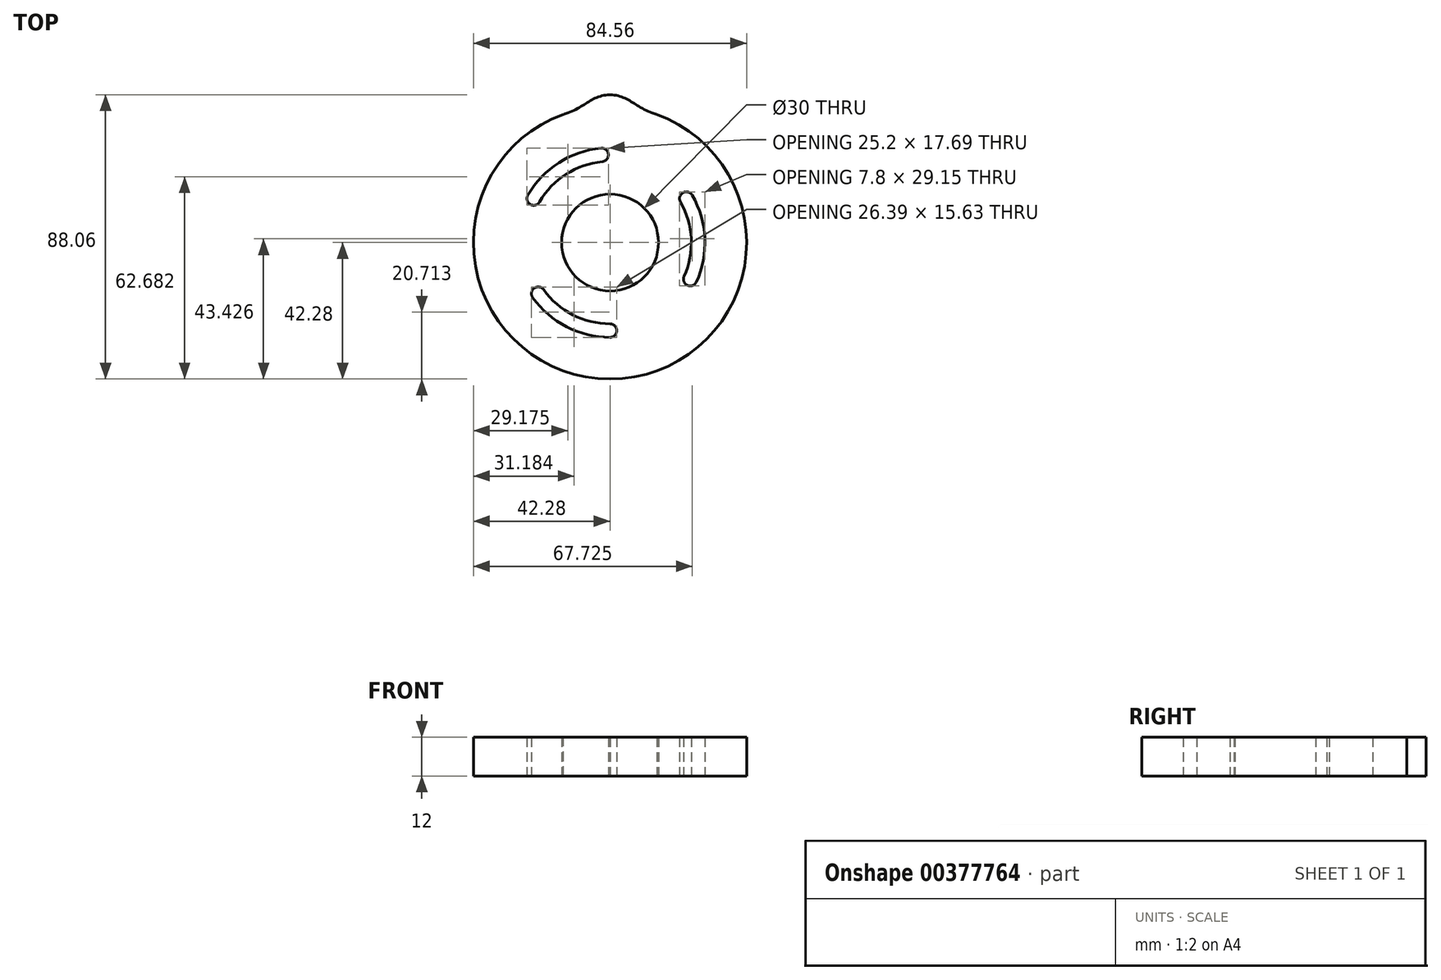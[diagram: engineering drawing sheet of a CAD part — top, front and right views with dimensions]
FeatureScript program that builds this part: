
annotation { "Feature Type Name" : "Feature", "Feature Type Description" : "" }
export const myFeature = defineFeature(function(context is Context, id is Id, definition is map)
    precondition{}
    {
        {
            var Q0;
            Q0=qCreatedBy(makeId("Top.planeOp"),FACE);
            var sketch = newSketch(context, id + "F0", { "sketchPlane" : qUnion([Q0])});
            skCircle(sketch, "E0", {"center": v(0, 0) * mm, "radius": 42.28 * mm});
            skCircle(sketch, "E1", {"center": v(0, 0) * mm, "radius": 15 * mm});
            skLineSegment(sketch, "E2", {"start": v(0, 42.28) * mm, "end": v(0, -42.28) * mm, "construction": true});
            skLineSegment(sketch, "E3", {"start": v(0, 0) * mm, "end": v(-14.46, 39.73) * mm, "construction": true});
            skLineSegment(sketch, "E4", {"start": v(0, 0) * mm, "end": v(14.46, 39.73) * mm, "construction": true});
            skLineSegment(sketch, "E5", {"start": v(0, 42.28) * mm, "end": v(0, 45.78) * mm, "construction": true});
            skFitSpline(sketch, "E6", {"points": [v(0, 45.78) * mm, v(-14.46, 39.73) * mm], "startDerivative": vector(-17.86, -0.27) * mm, "endDerivative": vector(-19.75, -5.43) * mm});
            skFitSpline(sketch, "E7.MirrorCS", {"points": [v(0, 45.78) * mm, v(14.46, 39.73) * mm], "startDerivative": vector(17.86, -0.27) * mm, "endDerivative": vector(19.75, -5.43) * mm});
            skLineSegment(sketch, "E8", {"start": v(0, 0) * mm, "end": v(36.61, 21.14) * mm, "construction": true});
            skLineSegment(sketch, "E9", {"start": v(0, 0) * mm, "end": v(-36.45, 21.04) * mm, "construction": true});
            skArc(sketch, "E10", {"start": v(-23.62, 13.64) * mm, "mid": v(-14.75, 22.95) * mm, "end": v(-2.6, 27.16) * mm, "construction": true});
            skArc(sketch, "E11", {"start": v(23.62, 13.64) * mm, "mid": v(27.25, 1.3) * mm, "end": v(24.81, -11.33) * mm, "construction": true});
            skArc(sketch, "E12", {"start": v(0, -27.28) * mm, "mid": v(-12.5, -24.25) * mm, "end": v(-22.22, -15.82) * mm, "construction": true});
            skArc(sketch, "E13.0.startCap", {"start": v(-21.8, 12.59) * mm, "mid": v(-24.67, 11.82) * mm, "end": v(-25.44, 14.69) * mm});
            skArc(sketch, "E13.0.endCap", {"start": v(-2.8, 29.25) * mm, "mid": v(-0.5, 27.36) * mm, "end": v(-2.4, 25.07) * mm});
            skArc(sketch, "E13.0.left", {"start": v(-25.44, 14.69) * mm, "mid": v(-15.88, 24.72) * mm, "end": v(-2.8, 29.25) * mm});
            skArc(sketch, "E13.0.right", {"start": v(-21.8, 12.59) * mm, "mid": v(-13.61, 21.18) * mm, "end": v(-2.4, 25.07) * mm});
            skArc(sketch, "E13.1.startCap", {"start": v(21.8, 12.59) * mm, "mid": v(22.57, 15.46) * mm, "end": v(25.44, 14.69) * mm});
            skArc(sketch, "E13.1.endCap", {"start": v(26.72, -12.2) * mm, "mid": v(23.94, -13.24) * mm, "end": v(22.9, -10.46) * mm});
            skArc(sketch, "E13.1.left", {"start": v(25.44, 14.69) * mm, "mid": v(29.35, 1.4) * mm, "end": v(26.72, -12.2) * mm});
            skArc(sketch, "E13.1.right", {"start": v(21.8, 12.59) * mm, "mid": v(25.15, 1.2) * mm, "end": v(22.9, -10.46) * mm});
            skArc(sketch, "E13.2.startCap", {"start": v(0, -25.18) * mm, "mid": v(2.1, -27.28) * mm, "end": v(0, -29.38) * mm});
            skArc(sketch, "E13.2.endCap", {"start": v(-23.93, -17.04) * mm, "mid": v(-23.44, -14.11) * mm, "end": v(-20.51, -14.6) * mm});
            skArc(sketch, "E13.2.left", {"start": v(0, -29.38) * mm, "mid": v(-13.46, -26.11) * mm, "end": v(-23.93, -17.04) * mm});
            skArc(sketch, "E13.2.right", {"start": v(0, -25.18) * mm, "mid": v(-11.54, -22.38) * mm, "end": v(-20.51, -14.6) * mm});
            skSolve(sketch);
        }
        {
            var Q0;
            Q0=makeQuery(id+"F0.imprint","IMPRINT",FACE,{"disambiguationData":[TD([[makeQuery(id+"F0.imprint","IMPRINT",EDGE,{"derivedFrom":sQuery(id+"F0.wireOp",EDGE,"E1")}),-1.0]])]});
            var Q1;
            {var subQ0=sQuery(id+"F0.wireOp",EDGE,"E7.MirrorCS");var subQ1=sQuery(id+"F0.wireOp",EDGE,"E0");var subQ2=makeQuery(id+"F0.imprint","INTERSECT",VERTEX,{"disambiguationData":[OD(1.0)],"derivedFrom":[subQ1,subQ0]});Q1=makeQuery(id+"F0.imprint","IMPRINT",FACE,{"disambiguationData":[TD([[makeQuery(id+"F0.imprint","IMPRINT",EDGE,{"disambiguationData":[TD([[subQ2,-1.0]])],"derivedFrom":subQ1}),-1.0]])]});}
            extrude(context, id + "F1", {"entities" : qUnion([Q0, Q1]), "depth" : 12 * mm});
        }
    });
